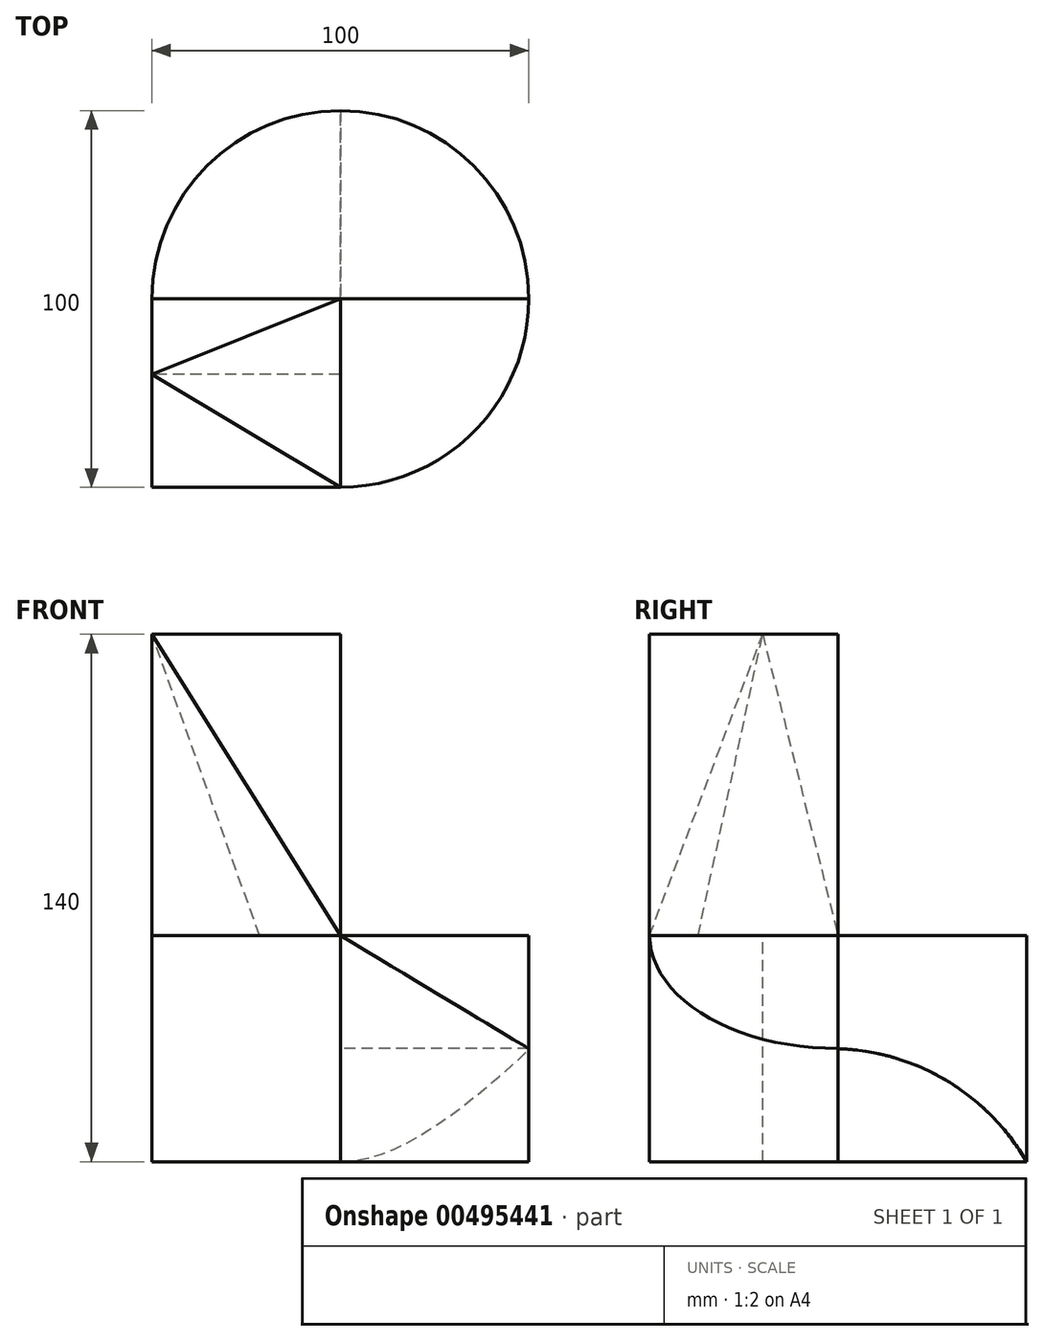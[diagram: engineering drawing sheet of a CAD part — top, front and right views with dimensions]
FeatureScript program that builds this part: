
annotation { "Feature Type Name" : "Feature", "Feature Type Description" : "" }
export const myFeature = defineFeature(function(context is Context, id is Id, definition is map)
    precondition{}
    {
        {
            var Q0;
            Q0=qCreatedBy(makeId("Top.planeOp"),FACE);
            var sketch = newSketch(context, id + "F0", { "sketchPlane" : qUnion([Q0])});
            skCircle(sketch, "E0", {"center": v(0, 0) * mm, "radius": 50 * mm});
            skSolve(sketch);
        }
        {
            var Q0;
            Q0 = qSketchRegion(id + "F0", true);
            extrude(context, id + "F1", {"entities" : qUnion([Q0]), "depth" : 60 * mm, "offsetDistance" : 25 * mm});
        }
        {
            var Q0;
            Q0=makeQuery(id+"F1.opExtrude","CAP_FACE",FACE,{"disambiguationData":[OSD([sQuery(id+"F0.wireOp",EDGE,"E0")])],"isStart":true});
            var sketch = newSketch(context, id + "F2", { "sketchPlane" : qUnion([Q0])});
            skLineSegment(sketch, "E1.bottom", {"start": v(0, 0) * mm, "end": v(-50, 0) * mm});
            skLineSegment(sketch, "E1.top", {"start": v(0, 50) * mm, "end": v(-50, 50) * mm});
            skLineSegment(sketch, "E1.left", {"start": v(0, 0) * mm, "end": v(0, 50) * mm});
            skLineSegment(sketch, "E1.right", {"start": v(-50, 0) * mm, "end": v(-50, 50) * mm});
            skSolve(sketch);
        }
        {
            var Q0;
            {var subQ0=sQuery(id+"F2.wireOp",EDGE,"E1.top");Q0=makeQuery(id+"F2.imprint","IMPRINT",FACE,{"disambiguationData":[TD([[makeQuery(id+"F2.imprint","IMPRINT",EDGE,{"derivedFrom":subQ0}),1.0]])]});}
            var Q1;
            {var subQ0=sQuery(id+"F2.wireOp",EDGE,"E1.bottom");Q1=makeQuery(id+"F2.imprint","IMPRINT",FACE,{"disambiguationData":[TD([[makeQuery(id+"F2.imprint","IMPRINT",EDGE,{"derivedFrom":subQ0}),-1.0]])]});}
            extrude(context, id + "F3", {"entities" : qUnion([Q0, Q1]), "operationType" : NewBodyOperationType.ADD, "oppositeDirection" : true, "depth" : 140 * mm, "offsetDistance" : 25 * mm});
        }
        {
            var Q0;
            Q0=makeQuery(id+"F3.opExtrude","SWEPT_FACE",FACE,{"disambiguationData":[OSD([sQuery(id+"F2.wireOp",EDGE,"E1.right")])]});
            var sketch = newSketch(context, id + "F4", { "sketchPlane" : qUnion([Q0])});
            skLineSegment(sketch, "E2.bottom", {"start": v(0, 0) * mm, "end": v(50, 0) * mm});
            skLineSegment(sketch, "E2.top", {"start": v(0, 60) * mm, "end": v(50, 60) * mm});
            skLineSegment(sketch, "E2.left", {"start": v(0, 0) * mm, "end": v(0, 60) * mm});
            skLineSegment(sketch, "E2.right", {"start": v(50, 0) * mm, "end": v(50, 60) * mm});
            skLineSegment(sketch, "E3", {"start": v(50, 0) * mm, "end": v(20, 0) * mm});
            skLineSegment(sketch, "E4", {"start": v(20, 0) * mm, "end": v(20, 60) * mm});
            skSolve(sketch);
        }
        {
            var Q0;
            {var subQ0=sQuery(id+"F4.wireOp",EDGE,"E2.right");Q0=makeQuery(id+"F4.imprint","IMPRINT",FACE,{"disambiguationData":[TD([[makeQuery(id+"F4.imprint","IMPRINT",EDGE,{"derivedFrom":subQ0}),-1.0]])]});}
            extrude(context, id + "F5", {"entities" : qUnion([Q0]), "operationType" : NewBodyOperationType.REMOVE, "oppositeDirection" : true, "depth" : 50 * mm, "offsetDistance" : 25 * mm});
        }
        {
            var Q0;
            Q0=makeQuery(id+"F3.opExtrude","CAP_FACE",FACE,{"disambiguationData":[OSD([sQuery(id+"F2.wireOp",EDGE,"E1.bottom"),sQuery(id+"F2.wireOp",EDGE,"E1.top"),sQuery(id+"F2.wireOp",EDGE,"E1.left"),sQuery(id+"F2.wireOp",EDGE,"E1.right")])],"isStart":false});
            var sketch = newSketch(context, id + "F6", { "sketchPlane" : qUnion([Q0])});
            skLineSegment(sketch, "E5.0", {"start": v(-0.01, -20) * mm, "end": v(-50, -20) * mm});
            skLineSegment(sketch, "E6", {"start": v(0, 0) * mm, "end": v(-50, -20) * mm});
            skLineSegment(sketch, "E7", {"start": v(0, -50) * mm, "end": v(-50, -20) * mm});
            skSolve(sketch);
        }
        {
            var Q1;
            Q1=makeQuery(id+"F3.opExtrude","SWEPT_FACE",FACE,{"disambiguationData":[OSD([sQuery(id+"F2.wireOp",EDGE,"E1.top")])]});
            var Q2;
            Q2=sQuery(id+"F6.wireOp",VERTEX,"E7.end");
            loft(context, id + "F7", {"operationType" : NewBodyOperationType.REMOVE, "sheetProfilesArray" : [{ "sheetProfileEntities" : qUnion([Q1]) }, { "sheetProfileEntities" : qUnion([Q2]) }]});
        }
        {
            var Q1;
            {var subQ0=sQuery(id+"F6.wireOp",EDGE,"E6");Q1=makeQuery(id+"F6.imprint","IMPRINT",FACE,{"disambiguationData":[TD([[makeQuery(id+"F6.imprint","IMPRINT",EDGE,{"derivedFrom":subQ0}),-1.0]])]});}
            var Q2;
            Q2=makeQuery(id+"F3.boolean.opBoolean","INTERSECT",VERTEX,{"derivedFrom":[makeQuery(id+"F1.opExtrude","CAP_FACE",FACE,{"disambiguationData":[OSD([sQuery(id+"F0.wireOp",EDGE,"E0")])],"isStart":false}),makeQuery(id+"F3.opExtrude","SWEPT_FACE",FACE,{"disambiguationData":[OSD([sQuery(id+"F2.wireOp",EDGE,"E1.bottom")])]}),makeQuery(id+"F3.opExtrude","SWEPT_FACE",FACE,{"disambiguationData":[OSD([sQuery(id+"F2.wireOp",EDGE,"E1.left")])]})]});
            loft(context, id + "F8", {"operationType" : NewBodyOperationType.REMOVE, "sheetProfilesArray" : [{ "sheetProfileEntities" : qUnion([Q1]) }, { "sheetProfileEntities" : qUnion([Q2]) }]});
        }
        {
            var Q0;
            Q0=qCreatedBy(makeId("Front.planeOp"),FACE);
            var sketch = newSketch(context, id + "F9", { "sketchPlane" : qUnion([Q0])});
            skLineSegment(sketch, "E8.bottom", {"start": v(0, 0) * mm, "end": v(50, 0) * mm});
            skLineSegment(sketch, "E8.top", {"start": v(0, 60) * mm, "end": v(50, 60) * mm});
            skLineSegment(sketch, "E8.left", {"start": v(0, 0) * mm, "end": v(0, 60) * mm});
            skLineSegment(sketch, "E8.right", {"start": v(50, 0) * mm, "end": v(50, 60) * mm});
            skLineSegment(sketch, "E9.bottom", {"start": v(0, 0) * mm, "end": v(-50, 0) * mm});
            skLineSegment(sketch, "E9.top", {"start": v(0, 60) * mm, "end": v(-50, 60) * mm});
            skLineSegment(sketch, "E9.right", {"start": v(-50, 0) * mm, "end": v(-50, 60) * mm});
            skLineSegment(sketch, "E10", {"start": v(0, 60) * mm, "end": v(50, 30) * mm});
            skLineSegment(sketch, "E11", {"start": v(50, 30) * mm, "end": v(50, 0) * mm});
            skSolve(sketch);
        }
        {
            var Q0;
            Q0=makeQuery(id+"F9.imprint","IMPRINT",FACE,{"disambiguationData":[TD([[makeQuery(id+"F9.imprint","IMPRINT",EDGE,{"derivedFrom":sQuery(id+"F9.wireOp",EDGE,"E8.top")}),-1.0]])]});
            extrude(context, id + "F10", {"entities" : qUnion([Q0]), "operationType" : NewBodyOperationType.REMOVE, "depth" : 72 * mm, "offsetDistance" : 25 * mm});
        }
        {
            var Q0;
            Q0=qCreatedBy(makeId("Right.planeOp"),FACE);
            var sketch = newSketch(context, id + "F11", { "sketchPlane" : qUnion([Q0])});
            skLineSegment(sketch, "E12.bottom", {"start": v(0, 0) * mm, "end": v(50, 0) * mm});
            skLineSegment(sketch, "E12.top", {"start": v(0, 60) * mm, "end": v(50, 60) * mm});
            skLineSegment(sketch, "E12.left", {"start": v(0, 0) * mm, "end": v(0, 60) * mm});
            skLineSegment(sketch, "E12.right", {"start": v(50, 0) * mm, "end": v(50, 60) * mm});
            skArc(sketch, "E13", {"start": v(50, 0) * mm, "mid": v(28.89, 21.48) * mm, "end": v(0, 29.99) * mm});
            skLineSegment(sketch, "E14", {"start": v(0, 29.99) * mm, "end": v(0, 0) * mm});
            skSolve(sketch);
        }
        {
            var Q0;
            Q0=makeQuery(id+"F11.imprint","IMPRINT",FACE,{"disambiguationData":[TD([[makeQuery(id+"F11.imprint","IMPRINT",EDGE,{"derivedFrom":sQuery(id+"F11.wireOp",EDGE,"E13")}),1.0]])]});
            extrude(context, id + "F12", {"entities" : qUnion([Q0]), "operationType" : NewBodyOperationType.REMOVE, "depth" : 64 * mm, "offsetDistance" : 25 * mm});
        }
    });
